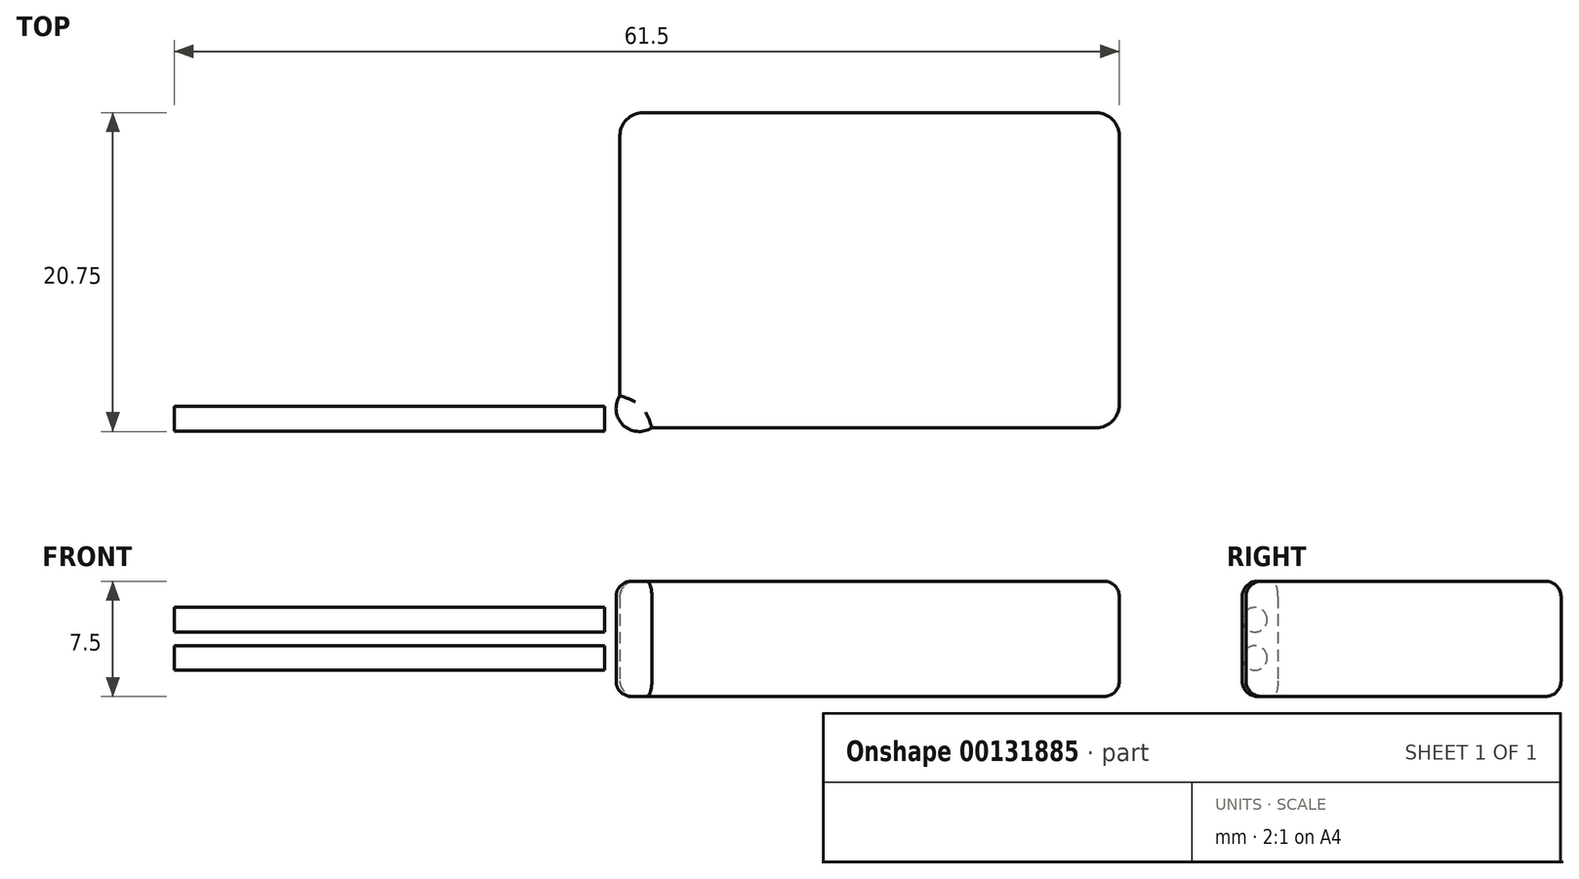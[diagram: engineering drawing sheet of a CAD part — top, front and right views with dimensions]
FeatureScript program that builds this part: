
annotation { "Feature Type Name" : "Feature", "Feature Type Description" : "" }
export const myFeature = defineFeature(function(context is Context, id is Id, definition is map)
    precondition{}
    {
        {
            var Q0;
            Q0=qCreatedBy(makeId("Top.planeOp"),FACE);
            var sketch = newSketch(context, id + "F0", { "sketchPlane" : qUnion([Q0])});
            skLineSegment(sketch, "E0.bottom", {"start": v(14.75, 10.25) * mm, "end": v(-14.75, 10.25) * mm});
            skLineSegment(sketch, "E0.top", {"start": v(14.75, -10.25) * mm, "end": v(-14.17, -10.25) * mm});
            skLineSegment(sketch, "E0.left", {"start": v(16.25, 8.75) * mm, "end": v(16.25, -8.75) * mm});
            skLineSegment(sketch, "E0.right", {"start": v(-16.25, 8.75) * mm, "end": v(-16.25, -8.17) * mm});
            skPoint(sketch, "E0.middle", {"position": v(0, 0) * mm});
            skArc(sketch, "E1", {"start": v(-16.25, -8.17) * mm, "mid": v(-16.06, -10.06) * mm, "end": v(-14.17, -10.25) * mm});
            skPoint(sketch, "E2.orphan", {"position": v(-16.25, -10.25) * mm});
            skPoint(sketch, "E3.visualSharp", {"position": v(-16.25, 10.25) * mm});
            skArc(sketch, "E3.filletArc", {"start": v(-14.75, 10.25) * mm, "mid": v(-15.81, 9.81) * mm, "end": v(-16.25, 8.75) * mm});
            skPoint(sketch, "E4.visualSharp", {"position": v(16.25, 10.25) * mm});
            skArc(sketch, "E4.filletArc", {"start": v(16.25, 8.75) * mm, "mid": v(15.81, 9.81) * mm, "end": v(14.75, 10.25) * mm});
            skPoint(sketch, "E5.visualSharp", {"position": v(16.25, -10.25) * mm});
            skArc(sketch, "E5.filletArc", {"start": v(14.75, -10.25) * mm, "mid": v(15.81, -9.81) * mm, "end": v(16.25, -8.75) * mm});
            skSolve(sketch);
        }
        {
            var Q0;
            Q0=makeQuery(id+"F0.imprint","IMPRINT",FACE,{"disambiguationData":[TD([[makeQuery(id+"F0.imprint","IMPRINT",EDGE,{"derivedFrom":sQuery(id+"F0.wireOp",EDGE,"E0.bottom")}),1.0]])]});
            extrude(context, id + "F1", {"entities" : qUnion([Q0]), "depth" : 7.5 * mm});
        }
        {
            var Q0;
            Q0=makeQuery(id+"F1.opExtrude","CAP_FACE",FACE,{"disambiguationData":[OSD([sQuery(id+"F0.wireOp",EDGE,"E0.bottom"),sQuery(id+"F0.wireOp",EDGE,"E0.top"),sQuery(id+"F0.wireOp",EDGE,"E0.left"),sQuery(id+"F0.wireOp",EDGE,"E0.right"),sQuery(id+"F0.wireOp",EDGE,"E1"),sQuery(id+"F0.wireOp",EDGE,"E3.filletArc"),sQuery(id+"F0.wireOp",EDGE,"E4.filletArc"),sQuery(id+"F0.wireOp",EDGE,"E5.filletArc")])],"isStart":false});
            var Q1;
            Q1=makeQuery(id+"F1.opExtrude","CAP_FACE",FACE,{"disambiguationData":[OSD([sQuery(id+"F0.wireOp",EDGE,"E0.bottom"),sQuery(id+"F0.wireOp",EDGE,"E0.top"),sQuery(id+"F0.wireOp",EDGE,"E0.left"),sQuery(id+"F0.wireOp",EDGE,"E0.right"),sQuery(id+"F0.wireOp",EDGE,"E1"),sQuery(id+"F0.wireOp",EDGE,"E3.filletArc"),sQuery(id+"F0.wireOp",EDGE,"E4.filletArc"),sQuery(id+"F0.wireOp",EDGE,"E5.filletArc")])],"isStart":true});
            fillet(context, id + "F2", {"entities" : qUnion([Q0, Q1]), "radius" : 1 * mm, "tangentPropagation" : true, "allowEdgeOverflow" : false});
        }
        {
            var Q0;
            Q0=makeQuery(id+"F1.opExtrude","SWEPT_FACE",FACE,{"disambiguationData":[OSD([sQuery(id+"F0.wireOp",EDGE,"E0.right")])]});
            cPlane(context, id + "F3", {"entities" : qUnion([Q0]), "cplaneType" : CPlaneType.OFFSET, "offset" : 1 * mm, "width" : 150 * mm, "height" : 150 * mm});
        }
        {
            var Q0;
            Q0=qCreatedBy(id+"F3.planeOp",FACE);
            var sketch = newSketch(context, id + "F4", { "sketchPlane" : qUnion([Q0])});
            skLineSegment(sketch, "E6", {"start": v(1.23, 3.75) * mm, "end": v(13.8, 3.75) * mm});
            skCircle(sketch, "E7", {"center": v(9.67, 2.5) * mm, "radius": 0.8 * mm});
            skCircle(sketch, "E8.MirrorC", {"center": v(9.67, 5) * mm, "radius": 0.8 * mm});
            skSolve(sketch);
        }
        {
            var Q0;
            Q0 = qSketchRegion(id + "F4", true);
            extrude(context, id + "F5", {"entities" : qUnion([Q0]), "operationType" : NewBodyOperationType.ADD, "depth" : 28 * mm});
        }
    });
